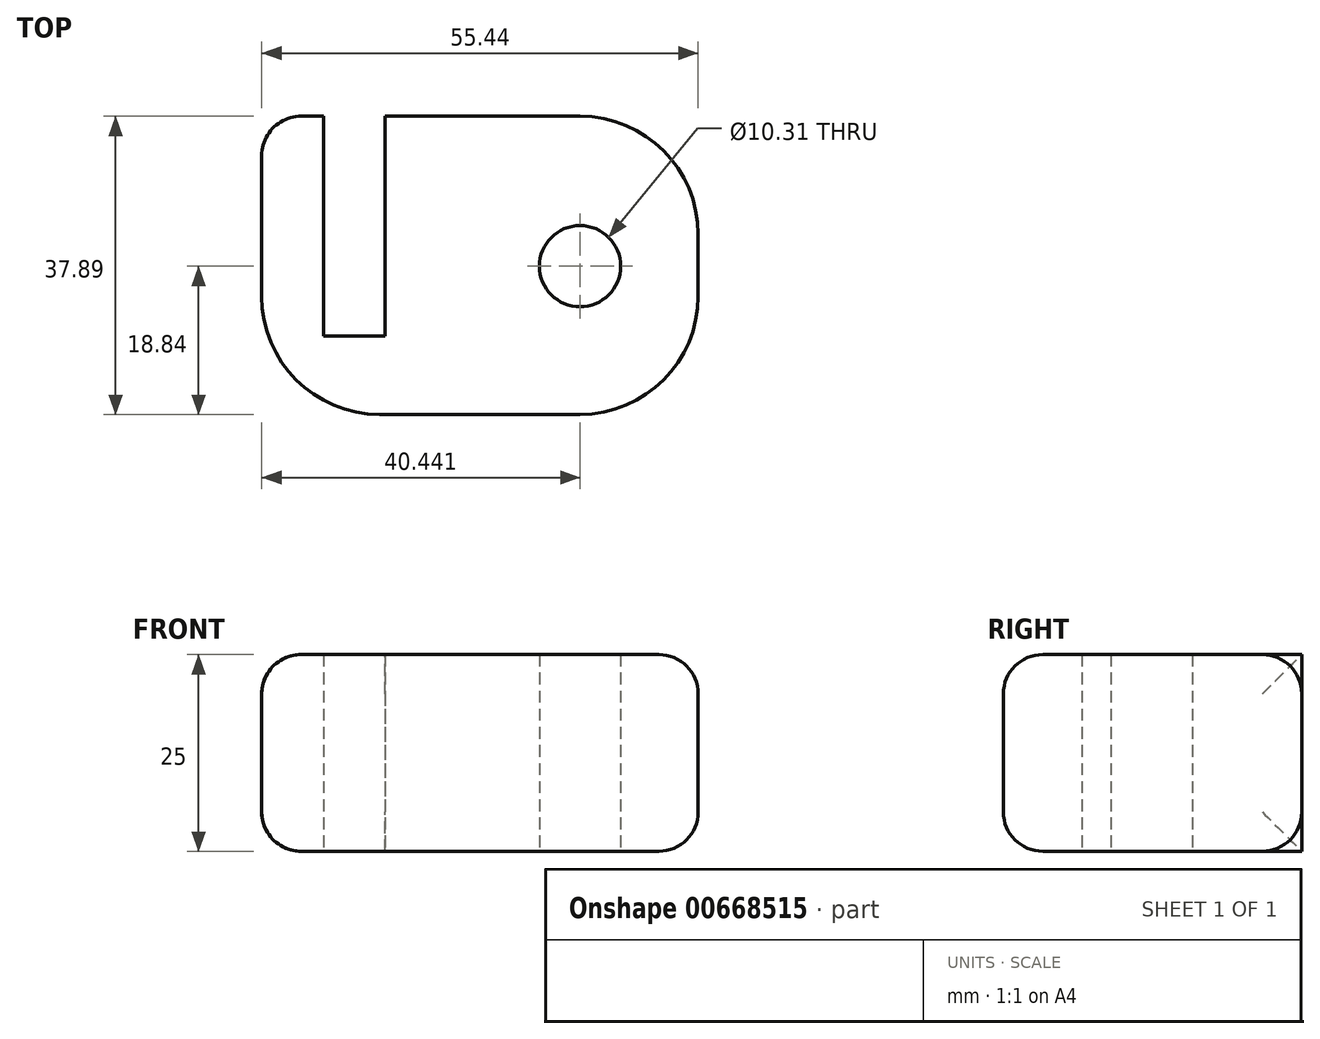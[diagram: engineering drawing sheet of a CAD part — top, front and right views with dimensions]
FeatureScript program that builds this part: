
annotation { "Feature Type Name" : "Feature", "Feature Type Description" : "" }
export const myFeature = defineFeature(function(context is Context, id is Id, definition is map)
    precondition{}
    {
        {
            var Q0;
            Q0=qCreatedBy(makeId("Top.planeOp"),FACE);
            var sketch = newSketch(context, id + "F0", { "sketchPlane" : qUnion([Q0])});
            skLineSegment(sketch, "E0.bottom", {"start": v(17.81, 22.32) * mm, "end": v(-22.63, 22.32) * mm});
            skLineSegment(sketch, "E0.top", {"start": v(17.81, -15.57) * mm, "end": v(-7.63, -15.57) * mm});
            skLineSegment(sketch, "E0.left", {"start": v(32.81, 7.32) * mm, "end": v(32.81, -0.57) * mm});
            skLineSegment(sketch, "E0.right", {"start": v(-22.63, 22.32) * mm, "end": v(-22.63, -0.57) * mm});
            skPoint(sketch, "E1.visualSharp", {"position": v(32.81, 22.32) * mm});
            skArc(sketch, "E1.filletArc", {"start": v(32.81, 7.32) * mm, "mid": v(28.42, 17.93) * mm, "end": v(17.81, 22.32) * mm});
            skPoint(sketch, "E2.visualSharp", {"position": v(32.81, -15.57) * mm});
            skArc(sketch, "E2.filletArc", {"start": v(17.81, -15.57) * mm, "mid": v(28.42, -11.17) * mm, "end": v(32.81, -0.57) * mm});
            skLineSegment(sketch, "E3.bottom", {"start": v(-14.78, 22.32) * mm, "end": v(-6.93, 22.32) * mm});
            skLineSegment(sketch, "E3.top", {"start": v(-14.78, -5.63) * mm, "end": v(-6.93, -5.63) * mm});
            skLineSegment(sketch, "E3.left", {"start": v(-14.78, 22.32) * mm, "end": v(-14.78, -5.63) * mm});
            skLineSegment(sketch, "E3.right", {"start": v(-6.93, 22.32) * mm, "end": v(-6.93, -5.63) * mm});
            skPoint(sketch, "E4.visualSharp", {"position": v(-22.63, -15.57) * mm});
            skArc(sketch, "E4.filletArc", {"start": v(-22.63, -0.57) * mm, "mid": v(-18.24, -11.17) * mm, "end": v(-7.63, -15.57) * mm});
            skCircle(sketch, "E5", {"center": v(17.81, 3.27) * mm, "radius": 5.15 * mm});
            skSolve(sketch);
        }
        {
            var Q0;
            Q0=makeQuery(id+"F0.imprint","IMPRINT",FACE,{"disambiguationData":[TD([[makeQuery(id+"F0.imprint","IMPRINT",EDGE,{"derivedFrom":sQuery(id+"F0.wireOp",EDGE,"E0.top")}),-1.0]])]});
            extrude(context, id + "F1", {"entities" : qUnion([Q0]), "depth" : 25 * mm, "offsetDistance" : 25 * mm});
        }
        {
            var Q0;
            {var subQ0=sQuery(id+"F0.wireOp",EDGE,"E0.bottom");Q0=makeQuery(id+"F1.opExtrude","CAP_EDGE",EDGE,{"disambiguationData":[OSD([subQ0]),TDD([makeQuery(id+"F0.imprint","IMPRINT",EDGE,{"disambiguationData":[TD([[makeQuery(id+"F0.imprint","INTERSECT",VERTEX,{"derivedFrom":[subQ0,sQuery(id+"F0.wireOp",EDGE,"E1.filletArc")]}),-1.0]])],"derivedFrom":subQ0})])],"isStart":true});}
            var Q1;
            {var subQ0=sQuery(id+"F0.wireOp",EDGE,"E0.bottom");Q1=makeQuery(id+"F1.opExtrude","CAP_EDGE",EDGE,{"disambiguationData":[OSD([subQ0]),TDD([makeQuery(id+"F0.imprint","IMPRINT",EDGE,{"disambiguationData":[TD([[makeQuery(id+"F0.imprint","INTERSECT",VERTEX,{"derivedFrom":[subQ0,sQuery(id+"F0.wireOp",EDGE,"E1.filletArc")]}),-1.0]])],"derivedFrom":subQ0})])],"isStart":false});}
            var Q2;
            Q2=makeQuery(id+"F1.opExtrude","SWEPT_EDGE",EDGE,{"disambiguationData":[OSD([sQuery(id+"F0.wireOp",EDGE,"E0.bottom"),sQuery(id+"F0.wireOp",EDGE,"E0.right")])]});
            fillet(context, id + "F2", {"entities" : qUnion([Q0, Q1, Q2]), "radius" : 5 * mm, "tangentPropagation" : true, "allowEdgeOverflow" : false});
        }
    });
